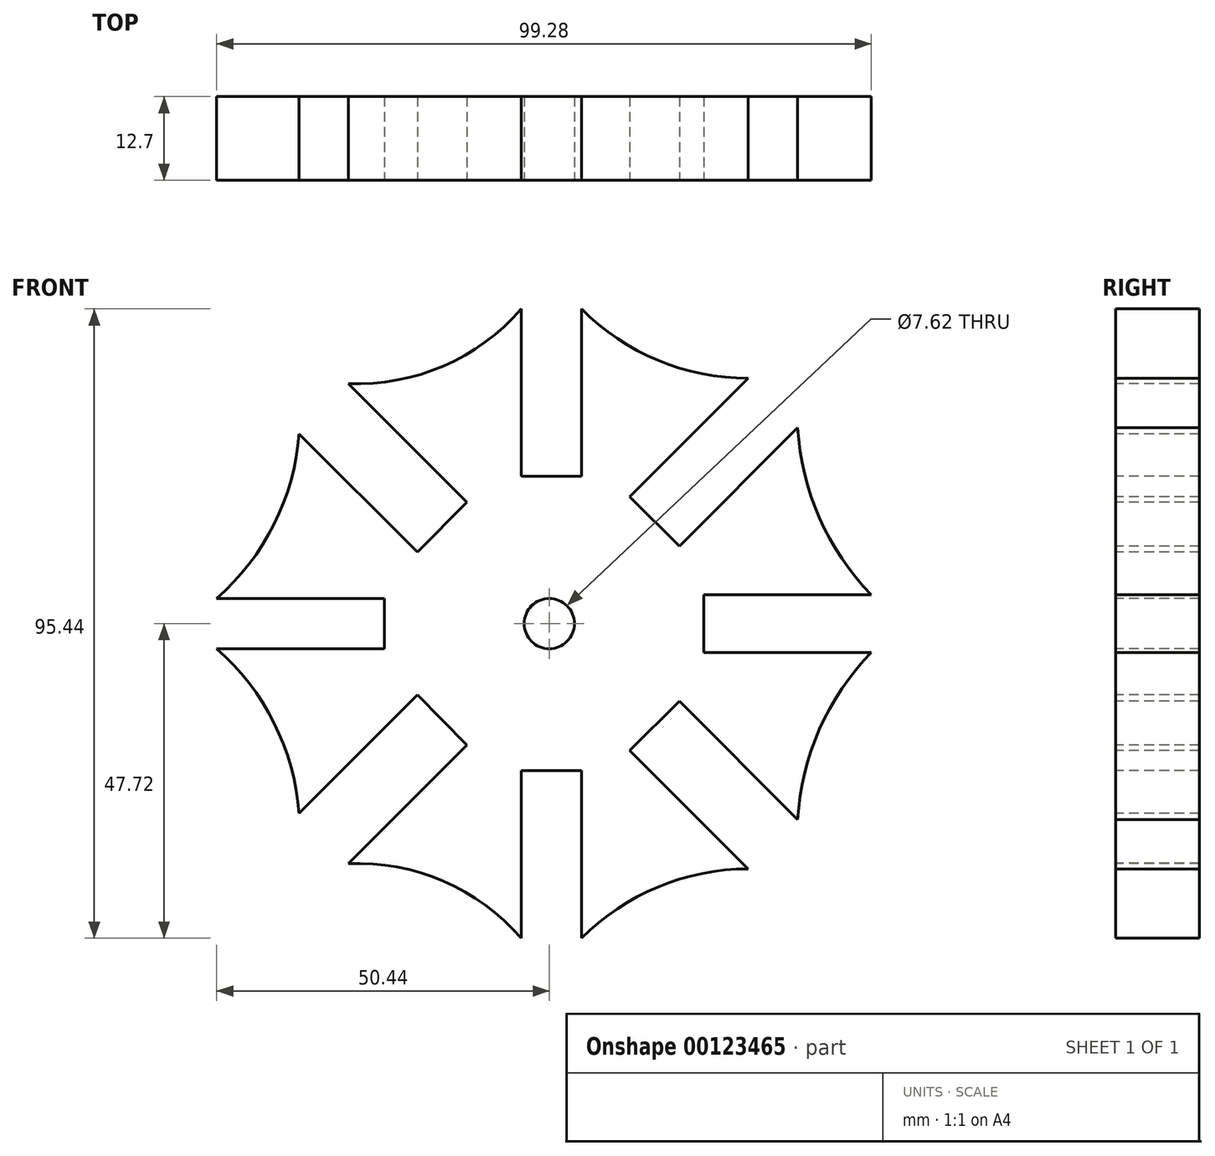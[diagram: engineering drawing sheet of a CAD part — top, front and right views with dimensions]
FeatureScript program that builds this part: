
annotation { "Feature Type Name" : "Feature", "Feature Type Description" : "" }
export const myFeature = defineFeature(function(context is Context, id is Id, definition is map)
    precondition{}
    {
        {
            var Q0;
            Q0=qCreatedBy(makeId("Front.planeOp"),FACE);
            var sketch = newSketch(context, id + "F0", { "sketchPlane" : qUnion([Q0])});
            skPoint(sketch, "E0.middle", {"position": v(0, 0) * mm});
            skPoint(sketch, "E1.startSnap0", {"position": v(-38.93, 0) * mm});
            skArc(sketch, "E2", {"start": v(-30.48, 36.39) * mm, "mid": v(-16.06, 39.06) * mm, "end": v(-4.23, 47.72) * mm});
            skArc(sketch, "E3", {"start": v(4.9, 47.72) * mm, "mid": v(16.49, 39.93) * mm, "end": v(30.2, 37.2) * mm});
            skArc(sketch, "E4", {"start": v(37.69, 29.7) * mm, "mid": v(40.98, 16.03) * mm, "end": v(48.84, 4.37) * mm});
            skArc(sketch, "E5", {"start": v(-50.44, 3.81) * mm, "mid": v(-41.74, 15.07) * mm, "end": v(-37.94, 28.79) * mm});
            skLineSegment(sketch, "E6", {"start": v(-4.23, 47.72) * mm, "end": v(-4.23, 22.32) * mm});
            skLineSegment(sketch, "E7", {"start": v(4.9, 47.72) * mm, "end": v(4.9, 22.32) * mm});
            skLineSegment(sketch, "E8", {"start": v(4.9, 22.32) * mm, "end": v(-4.23, 22.32) * mm});
            skLineSegment(sketch, "E9", {"start": v(30.2, 37.2) * mm, "end": v(12.23, 19.24) * mm});
            skLineSegment(sketch, "E10", {"start": v(37.69, 29.7) * mm, "end": v(19.73, 11.74) * mm});
            skLineSegment(sketch, "E11", {"start": v(-30.48, 36.39) * mm, "end": v(-12.51, 18.43) * mm});
            skLineSegment(sketch, "E12", {"start": v(-37.94, 28.79) * mm, "end": v(-19.98, 10.83) * mm});
            skLineSegment(sketch, "E13", {"start": v(-50.44, 3.8) * mm, "end": v(-25.04, 3.8) * mm});
            skLineSegment(sketch, "E14", {"start": v(-25.04, 3.8) * mm, "end": v(-25.04, 0) * mm});
            skLineSegment(sketch, "E15", {"start": v(-19.98, 10.83) * mm, "end": v(-12.51, 18.43) * mm});
            skLineSegment(sketch, "E16", {"start": v(12.23, 19.24) * mm, "end": v(19.73, 11.74) * mm});
            skLineSegment(sketch, "E17", {"start": v(48.84, 4.37) * mm, "end": v(23.44, 4.37) * mm});
            skLineSegment(sketch, "E18", {"start": v(23.44, 4.37) * mm, "end": v(23.44, 0) * mm});
            skLineSegment(sketch, "E19", {"start": v(0, 53.88) * mm, "end": v(0, -53.88) * mm, "construction": true});
            skLineSegment(sketch, "E20", {"start": v(-38.1, -38.1) * mm, "end": v(38.1, 38.1) * mm, "construction": true});
            skLineSegment(sketch, "E21", {"start": v(38.33, -37.67) * mm, "end": v(-38.33, 37.67) * mm, "construction": true});
            skLineSegment(sketch, "E22", {"start": v(-55.65, 0) * mm, "end": v(53.88, 0) * mm, "construction": true});
            skLineSegment(sketch, "E23.MirrorCS", {"start": v(-50.44, -3.81) * mm, "end": v(-48.26, -3.81) * mm});
            skLineSegment(sketch, "E24.MirrorCS", {"start": v(-37.94, -28.79) * mm, "end": v(-37.13, -27.97) * mm});
            skLineSegment(sketch, "E25.MirrorCS", {"start": v(-15.44, -15.44) * mm, "end": v(-12.51, -18.43) * mm});
            skPoint(sketch, "E26.MirrorCS.end.orphan", {"position": v(23.44, -4.37) * mm});
            skPoint(sketch, "E26.MirrorCS.start.orphan", {"position": v(48.84, -4.37) * mm});
            skPoint(sketch, "E27.MirrorCS.start.orphan", {"position": v(37.69, -29.7) * mm});
            skPoint(sketch, "E28.orphan", {"position": v(19.73, -11.74) * mm});
            skPoint(sketch, "E29.MirrorCS.start.orphan", {"position": v(30.2, -37.2) * mm});
            skPoint(sketch, "E30.start.orphan", {"position": v(12.23, -19.24) * mm});
            skPoint(sketch, "E31.orphan", {"position": v(-4.23, -22.32) * mm});
            skPoint(sketch, "E32.MirrorCS.start.orphan", {"position": v(4.9, -22.32) * mm});
            skPoint(sketch, "E33.MirrorCS.start.orphan", {"position": v(4.9, -47.72) * mm});
            skPoint(sketch, "E34.MirrorCS.start.orphan", {"position": v(-4.23, -47.72) * mm});
            skPoint(sketch, "E35.MirrorCS.end.orphan", {"position": v(-12.51, -18.43) * mm});
            skPoint(sketch, "E35.MirrorCS.start.orphan", {"position": v(-30.48, -36.39) * mm});
            skPoint(sketch, "E36.orphan", {"position": v(-19.98, -10.83) * mm});
            skPoint(sketch, "E37.orphan", {"position": v(-25.04, -3.81) * mm});
            skPoint(sketch, "E38.MirrorCS.end.orphan", {"position": v(-25.04, 0) * mm});
            skLineSegment(sketch, "E39.MirrorCS", {"start": v(-50.44, -3.81) * mm, "end": v(-25.04, -3.81) * mm});
            skLineSegment(sketch, "E40.MirrorCS", {"start": v(-25.04, -3.81) * mm, "end": v(-25.04, 0) * mm});
            skLineSegment(sketch, "E41.MirrorCS", {"start": v(-37.94, -28.79) * mm, "end": v(-19.98, -10.83) * mm});
            skLineSegment(sketch, "E42.MirrorCS", {"start": v(-19.98, -10.83) * mm, "end": v(-12.51, -18.43) * mm});
            skLineSegment(sketch, "E43.MirrorCS", {"start": v(-30.48, -36.39) * mm, "end": v(-12.51, -18.43) * mm});
            skLineSegment(sketch, "E44.MirrorCS", {"start": v(-4.23, -47.72) * mm, "end": v(-4.23, -22.32) * mm});
            skLineSegment(sketch, "E45.MirrorCS", {"start": v(4.9, -22.32) * mm, "end": v(-4.23, -22.32) * mm});
            skLineSegment(sketch, "E46.MirrorCS", {"start": v(4.9, -47.72) * mm, "end": v(4.9, -22.32) * mm});
            skLineSegment(sketch, "E47.MirrorCS", {"start": v(30.2, -37.2) * mm, "end": v(12.23, -19.24) * mm});
            skLineSegment(sketch, "E48.MirrorCS", {"start": v(12.23, -19.24) * mm, "end": v(19.73, -11.74) * mm});
            skLineSegment(sketch, "E49.MirrorCS", {"start": v(48.84, -4.37) * mm, "end": v(23.44, -4.37) * mm});
            skLineSegment(sketch, "E50.MirrorCS", {"start": v(23.44, -4.37) * mm, "end": v(23.44, 0) * mm});
            skArc(sketch, "E51.MirrorCS", {"start": v(37.69, -29.7) * mm, "mid": v(40.98, -16.03) * mm, "end": v(48.84, -4.37) * mm});
            skArc(sketch, "E52.MirrorCS", {"start": v(4.9, -47.72) * mm, "mid": v(16.49, -39.93) * mm, "end": v(30.2, -37.2) * mm});
            skArc(sketch, "E53.MirrorCS", {"start": v(-30.48, -36.39) * mm, "mid": v(-16.06, -39.06) * mm, "end": v(-4.23, -47.72) * mm});
            skArc(sketch, "E54.MirrorCS", {"start": v(-50.44, -3.81) * mm, "mid": v(-41.74, -15.07) * mm, "end": v(-37.94, -28.79) * mm});
            skLineSegment(sketch, "E55.MirrorCS", {"start": v(37.69, -29.7) * mm, "end": v(19.73, -11.74) * mm});
            skCircle(sketch, "E56", {"center": v(0, 0) * mm, "radius": 3.81 * mm});
            skSolve(sketch);
        }
        {
            var Q0;
            Q0=makeQuery(id+"F0.imprint","IMPRINT",FACE,{"disambiguationData":[TD([[makeQuery(id+"F0.imprint","IMPRINT",EDGE,{"derivedFrom":sQuery(id+"F0.wireOp",EDGE,"E2")}),-1.0]])]});
            extrude(context, id + "F1", {"entities" : qUnion([Q0]), "oppositeDirection" : true, "depth" : 12.7 * mm});
        }
    });
